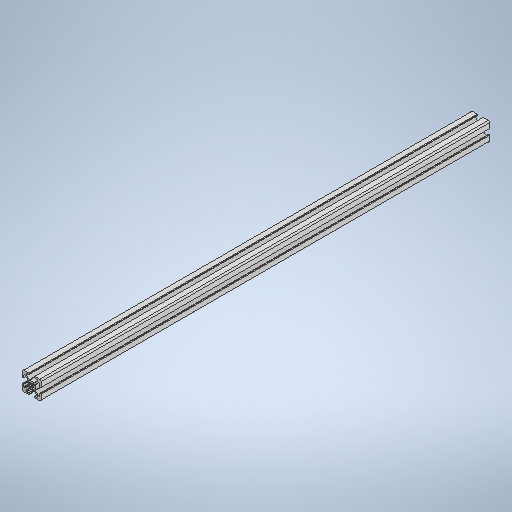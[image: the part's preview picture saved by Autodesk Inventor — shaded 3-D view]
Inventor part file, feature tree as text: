
AUTODESK INVENTOR PART (.ipt)
format: ipt  version: 2025 (Build 290162000, 162)  size: 371,712 bytes
history: native  units: mm
features: extrude x1, sketch x1
ambient origin geometry x8: Origin, YZ Plane, XZ Plane, XY Plane, X Axis, Y Axis, Z Axis, Center Point
bodies: Solid1 (feature_tree)
feature tree (2):
  extrude  "Extrusion1"  Depth=481.0mm
  sketch  "Sketch1"  dims[d0=481.0mm d1=0.0mm d2=1.0mm d3=1.0mm d4=1.0mm d5=0.15mm d6=0.25mm d7=0.375mm d8=14.3117mm d9=0.75mm d10=20.594885mm d11=0.0625mm d12=0.75mm d13=0.375mm]
